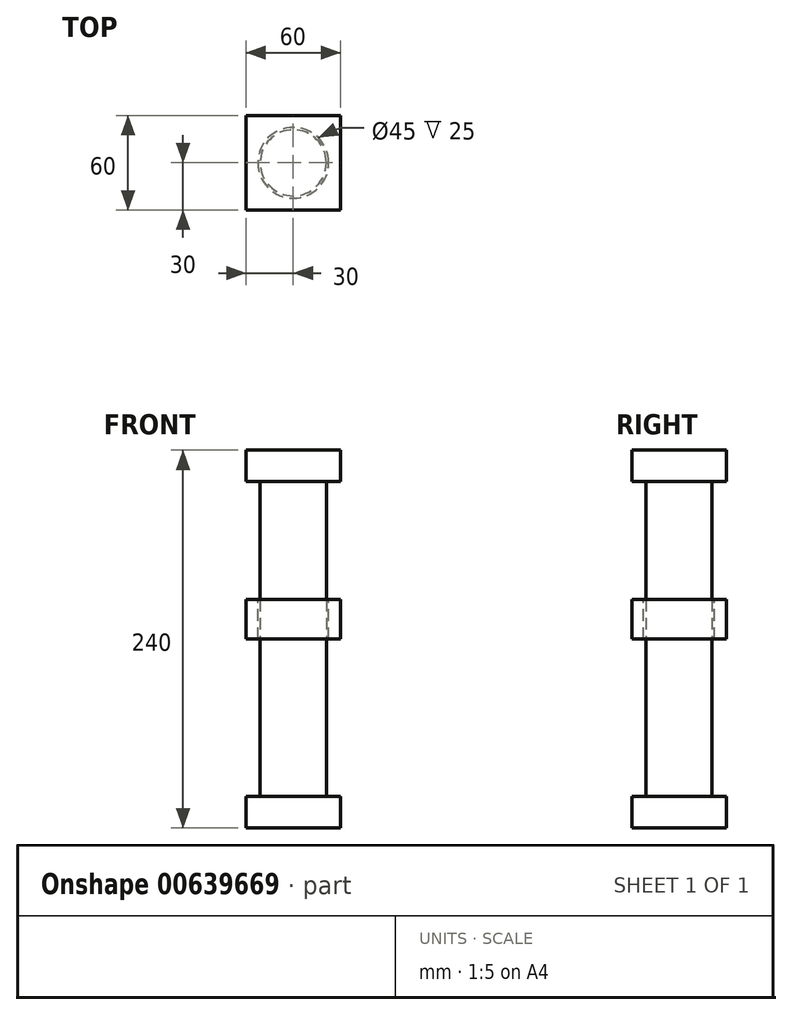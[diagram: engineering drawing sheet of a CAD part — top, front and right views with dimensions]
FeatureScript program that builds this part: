
annotation { "Feature Type Name" : "Feature", "Feature Type Description" : "" }
export const myFeature = defineFeature(function(context is Context, id is Id, definition is map)
    precondition{}
    {
        {
            var Q0;
            Q0=qCreatedBy(makeId("Top.planeOp"),FACE);
            var sketch = newSketch(context, id + "F0", { "sketchPlane" : qUnion([Q0])});
            skLineSegment(sketch, "E0.bottom", {"start": v(-30, 30) * mm, "end": v(30, 30) * mm});
            skLineSegment(sketch, "E0.top", {"start": v(-30, -30) * mm, "end": v(30, -30) * mm});
            skLineSegment(sketch, "E0.left", {"start": v(-30, 30) * mm, "end": v(-30, -30) * mm});
            skLineSegment(sketch, "E0.right", {"start": v(30, 30) * mm, "end": v(30, -30) * mm});
            skPoint(sketch, "E0.middle", {"position": v(0, 0) * mm});
            skSolve(sketch);
        }
        {
            var Q0;
            Q0=makeQuery(id+"F0.imprint","IMPRINT",FACE,{"disambiguationData":[TD([[makeQuery(id+"F0.imprint","IMPRINT",EDGE,{"derivedFrom":sQuery(id+"F0.wireOp",EDGE,"E0.bottom")}),-1.0]])]});
            extrude(context, id + "F1", {"entities" : qUnion([Q0]), "depth" : 25 * mm, "offsetDistance" : 25 * mm});
        }
        {
            var Q0;
            Q0=makeQuery(id+"F1.opExtrude","CAP_FACE",FACE,{"disambiguationData":[OSD([sQuery(id+"F0.wireOp",EDGE,"E0.bottom"),sQuery(id+"F0.wireOp",EDGE,"E0.top"),sQuery(id+"F0.wireOp",EDGE,"E0.left"),sQuery(id+"F0.wireOp",EDGE,"E0.right")])],"isStart":false});
            var sketch = newSketch(context, id + "F2", { "sketchPlane" : qUnion([Q0])});
            skCircle(sketch, "E1", {"center": v(0, 0) * mm, "radius": 22.5 * mm});
            skSolve(sketch);
        }
        {
            var Q0;
            Q0=makeQuery(id+"F2.imprint","IMPRINT",FACE,{"disambiguationData":[TD([[makeQuery(id+"F2.imprint","IMPRINT",EDGE,{"derivedFrom":sQuery(id+"F2.wireOp",EDGE,"E1")}),1.0]])]});
            extrude(context, id + "F3", {"entities" : qUnion([Q0]), "operationType" : NewBodyOperationType.REMOVE, "endBound" : BoundingType.THROUGH_ALL, "oppositeDirection" : true, "depth" : 25 * mm, "offsetDistance" : 25 * mm});
        }
        {
            var Q0;
            Q0=qCreatedBy(makeId("Top.planeOp"),FACE);
            var sketch = newSketch(context, id + "F4", { "sketchPlane" : qUnion([Q0])});
            skCircle(sketch, "E2", {"center": v(0, 0) * mm, "radius": 21 * mm});
            skSolve(sketch);
        }
        {
            var Q0;
            Q0=makeQuery(id+"F4.imprint","IMPRINT",FACE,{"disambiguationData":[TD([[makeQuery(id+"F4.imprint","IMPRINT",EDGE,{"derivedFrom":sQuery(id+"F4.wireOp",EDGE,"E2")}),1.0]])]});
            extrude(context, id + "F5", {"entities" : qUnion([Q0]), "endBound" : BoundingType.SYMMETRIC, "depth" : 200 * mm, "offsetDistance" : 25 * mm});
        }
        {
            var Q0;
            Q0=makeQuery(id+"F5.opExtrude","CAP_FACE",FACE,{"disambiguationData":[OSD([sQuery(id+"F4.wireOp",EDGE,"E2")])],"isStart":false});
            var sketch = newSketch(context, id + "F6", { "sketchPlane" : qUnion([Q0])});
            skLineSegment(sketch, "E3.bottom", {"start": v(30, -30) * mm, "end": v(-30, -30) * mm});
            skLineSegment(sketch, "E3.top", {"start": v(30, 30) * mm, "end": v(-30, 30) * mm});
            skLineSegment(sketch, "E3.left", {"start": v(30, -30) * mm, "end": v(30, 30) * mm});
            skLineSegment(sketch, "E3.right", {"start": v(-30, -30) * mm, "end": v(-30, 30) * mm});
            skPoint(sketch, "E3.middle", {"position": v(0, 0) * mm});
            skSolve(sketch);
        }
        {
            var Q0;
            Q0=makeQuery(id+"F6.imprint","IMPRINT",FACE,{"disambiguationData":[TD([[makeQuery(id+"F6.imprint","IMPRINT",EDGE,{"derivedFrom":makeQuery(id+"F5.opExtrude","CAP_EDGE",EDGE,{"disambiguationData":[OSD([sQuery(id+"F4.wireOp",EDGE,"E2")])],"isStart":false})}),1.0]])]});
            var Q1;
            Q1=makeQuery(id+"F6.imprint","IMPRINT",FACE,{"disambiguationData":[TD([[makeQuery(id+"F6.imprint","IMPRINT",EDGE,{"derivedFrom":sQuery(id+"F6.wireOp",EDGE,"E3.bottom")}),-1.0]])]});
            extrude(context, id + "F7", {"entities" : qUnion([Q0, Q1]), "operationType" : NewBodyOperationType.ADD, "depth" : 20 * mm, "offsetDistance" : 25 * mm});
        }
        {
            var Q0;
            Q0=makeQuery(id+"F5.opExtrude","CAP_FACE",FACE,{"disambiguationData":[OSD([sQuery(id+"F4.wireOp",EDGE,"E2")])],"isStart":true});
            var sketch = newSketch(context, id + "F8", { "sketchPlane" : qUnion([Q0])});
            skLineSegment(sketch, "E4.bottom", {"start": v(30, -30) * mm, "end": v(-30, -30) * mm});
            skLineSegment(sketch, "E4.top", {"start": v(30, 30) * mm, "end": v(-30, 30) * mm});
            skLineSegment(sketch, "E4.left", {"start": v(30, -30) * mm, "end": v(30, 30) * mm});
            skLineSegment(sketch, "E4.right", {"start": v(-30, -30) * mm, "end": v(-30, 30) * mm});
            skPoint(sketch, "E4.middle", {"position": v(0, 0) * mm});
            skSolve(sketch);
        }
        {
            var Q0;
            Q0=makeQuery(id+"F8.imprint","IMPRINT",FACE,{"disambiguationData":[TD([[makeQuery(id+"F8.imprint","IMPRINT",EDGE,{"derivedFrom":makeQuery(id+"F5.opExtrude","CAP_EDGE",EDGE,{"disambiguationData":[OSD([sQuery(id+"F4.wireOp",EDGE,"E2")])],"isStart":true})}),-1.0]])]});
            var Q1;
            Q1=makeQuery(id+"F8.imprint","IMPRINT",FACE,{"disambiguationData":[TD([[makeQuery(id+"F8.imprint","IMPRINT",EDGE,{"derivedFrom":sQuery(id+"F8.wireOp",EDGE,"E4.bottom")}),-1.0]])]});
            extrude(context, id + "F9", {"entities" : qUnion([Q0, Q1]), "operationType" : NewBodyOperationType.ADD, "depth" : 20 * mm, "offsetDistance" : 25 * mm});
        }
    });
